# Revit family: FU_Table_Sandler_Bau Table
name_source: partatom
category: Furniture
units: mm (PartAtom-declared; Revit-internal decimal feet)

## family parameters
Always vertical = Yes
Cut with Voids When Loaded = No
OmniClass Number = 23.40.20.00
OmniClass Title = General Furniture and Specialties
Room Calculation Point = No
Shared = No
Work Plane-Based = No

## types (1)
- Bau Connecting Table with Linking Device
    Default Elevation = 0 mm  [stored 0 ft]
    Depth = 490 mm  [stored 1.60761 ft]
    Description = 30cm x 49cm / 12″ x 19″ linking table in steel finished in textured powdercoat.
    Height = 182 mm  [stored 0.597113 ft]
    Manufacturer = Sandler
    Model = Bau Connecting Table with Linking Device
    Top Finish = Textured Powdercoats - 891 White Grey
    URL = https://www.sandlerseating.com
    Width = 300 mm

note: [stored X ft] marks values corroborated as IEEE doubles in the binary element streams (Revit-internal decimal feet)

## geometry (parser evidence)
native form markers: Sweep x6
no freeform markers — native parametric forms only
